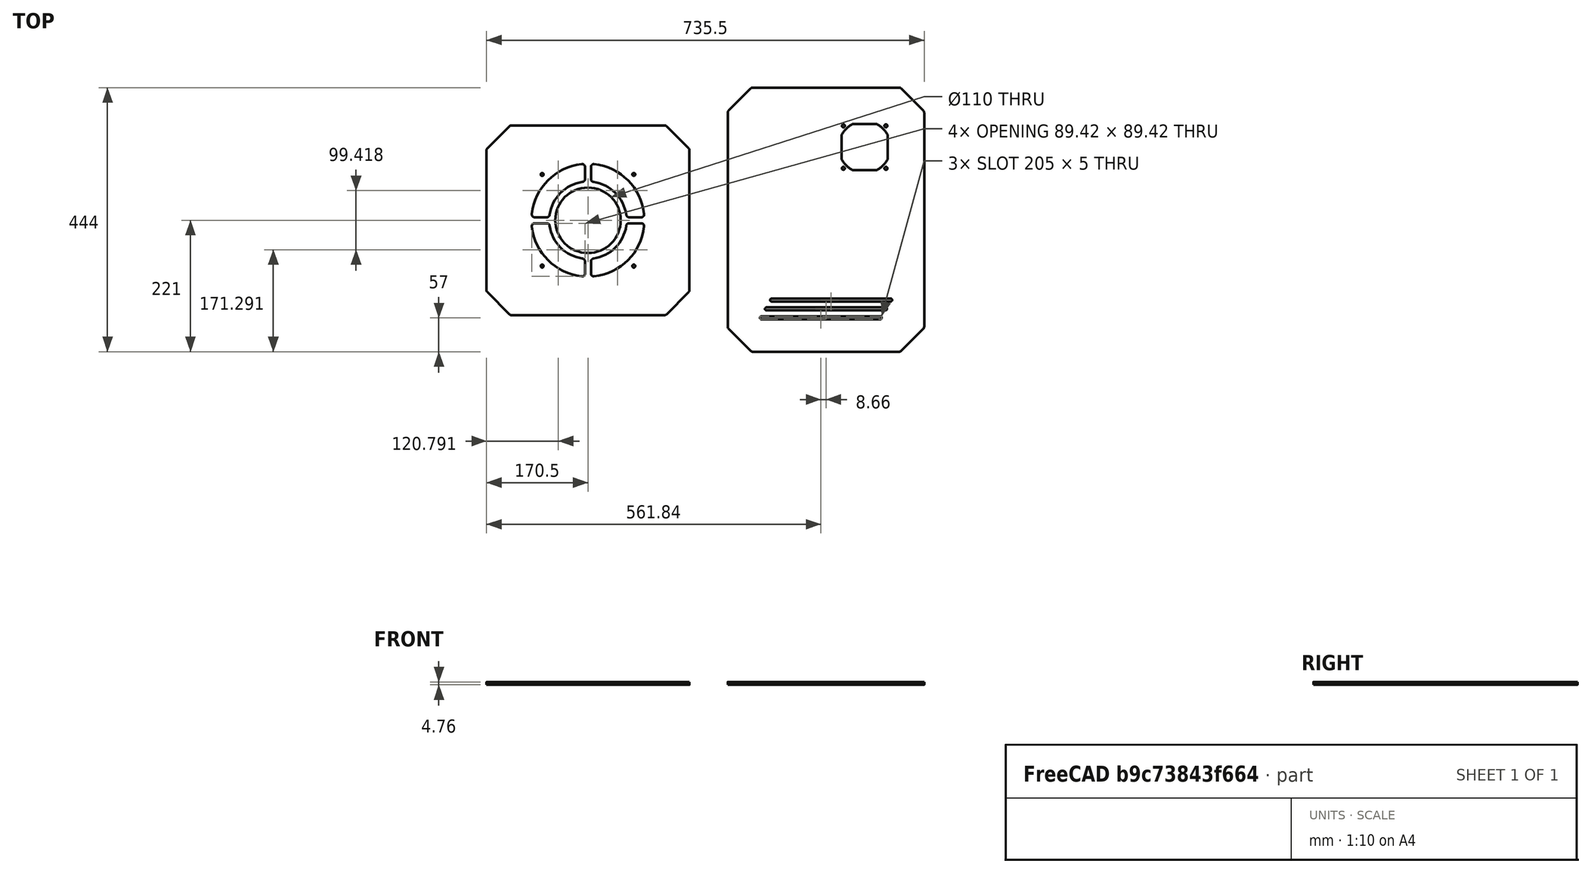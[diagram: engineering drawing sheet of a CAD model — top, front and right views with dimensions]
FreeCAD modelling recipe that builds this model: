
FCSTD DOCUMENT  (FreeCAD 0.19R23578 (Git))
Label: enclosure_windows
License: All rights reserved
LicenseURL: http://en.wikipedia.org/wiki/All_rights_reserved
objects: TechDraw::DrawViewDimExtent×4, PartDesign::CoordinateSystem×4, Sketcher::SketchObject×2, TechDraw::DrawViewPart×2, PartDesign::Pad×2, TechDraw::DrawRichAnno×2, PartDesign::Body×2, TechDraw::DrawSVGTemplate×1, PartDesign::Fillet×1, TechDraw::DrawPage×1
note: 14 computed .brp shape members not serialized (recipe doc carries the construction recipe); baked Part::Feature solids carry a one-line shape summary decoded from their .brp

FEATURE [Sketcher::SketchObject] Sketch001  label="side_piece"
  AttachmentOffset = pos=(400,1,0) rot=(0,0,1;0rad)
  MapMode = 5
  Placement = pos=(400,1,0) rot=(0,0,1;0rad)
  Support = -> [XY_Plane]
  sketch-geometry (52):
    g0: LineSegment StartX=-165 StartY=180 StartZ=0 EndX=-165 EndY=-180 EndZ=0
    g1: LineSegment StartX=-163.536 StartY=-183.536 StartZ=0 EndX=-126.536 EndY=-220.536 EndZ=0
    g2: LineSegment StartX=-123 StartY=-222 StartZ=0 EndX=123 EndY=-222 EndZ=0
    g3: LineSegment StartX=126.536 StartY=-220.536 StartZ=0 EndX=163.536 EndY=-183.536 EndZ=0
    g4: LineSegment StartX=165 StartY=-180 StartZ=0 EndX=165 EndY=180 EndZ=0
    g5: LineSegment StartX=163.536 StartY=183.536 StartZ=0 EndX=126.536 EndY=220.536 EndZ=0
    g6: LineSegment StartX=123 StartY=222 StartZ=0 EndX=-123 EndY=222 EndZ=0
    g7: LineSegment StartX=-126.536 StartY=220.536 StartZ=0 EndX=-163.536 EndY=183.536 EndZ=0
    g8: LineSegment StartX=-108.66 StartY=-165 StartZ=0 EndX=-91.3397 EndY=-135 EndZ=0
    g9: LineSegment StartX=-91.3397 StartY=-135 StartZ=0 EndX=108.66 EndY=-135 EndZ=0
    g10: LineSegment StartX=91.3397 StartY=-165 StartZ=0 EndX=-108.66 EndY=-165 EndZ=0
    g11: ArcOfCircle CenterX=-91.3397 CenterY=-135 CenterZ=0 NormalX=0 NormalY=0 NormalZ=1 AngleXU=0 Radius=2.5 StartAngle=1.5708 EndAngle=4.71239
    g12: ArcOfCircle CenterX=108.66 CenterY=-135 CenterZ=0 NormalX=0 NormalY=0 NormalZ=1 AngleXU=0 Radius=2.5 StartAngle=4.71239 EndAngle=7.85398
    g13: LineSegment StartX=-91.3397 StartY=-137.5 StartZ=0 EndX=108.66 EndY=-137.5 EndZ=0
    g14: LineSegment StartX=-91.3397 StartY=-132.5 StartZ=0 EndX=108.66 EndY=-132.5 EndZ=0
    g15: ArcOfCircle CenterX=-100 CenterY=-150 CenterZ=0 NormalX=0 NormalY=0 NormalZ=1 AngleXU=0 Radius=2.5 StartAngle=1.5708 EndAngle=4.71239
    g16: ArcOfCircle CenterX=100 CenterY=-150 CenterZ=0 NormalX=0 NormalY=0 NormalZ=1 AngleXU=0 Radius=2.5 StartAngle=4.71239 EndAngle=7.85398
    g17: LineSegment StartX=-100 StartY=-152.5 StartZ=0 EndX=100 EndY=-152.5 EndZ=0
    g18: LineSegment StartX=-100 StartY=-147.5 StartZ=0 EndX=100 EndY=-147.5 EndZ=0
    g19: ArcOfCircle CenterX=-108.66 CenterY=-165 CenterZ=0 NormalX=0 NormalY=0 NormalZ=1 AngleXU=0 Radius=2.5 StartAngle=1.5708 EndAngle=4.71239
    g20: ArcOfCircle CenterX=91.3397 CenterY=-165 CenterZ=0 NormalX=0 NormalY=0 NormalZ=1 AngleXU=0 Radius=2.5 StartAngle=4.71239 EndAngle=7.85398
    g21: LineSegment StartX=-108.66 StartY=-167.5 StartZ=0 EndX=91.3397 EndY=-167.5 EndZ=0
    g22: LineSegment StartX=-108.66 StartY=-162.5 StartZ=0 EndX=91.3397 EndY=-162.5 EndZ=0
    g23: LineSegment StartX=44.2199 StartY=160.5 StartZ=0 EndX=85.7801 EndY=160.5 EndZ=0
    g24: LineSegment StartX=103.5 StartY=101.22 StartZ=0 EndX=103.5 EndY=142.78 EndZ=0
    g25: LineSegment StartX=85.7801 StartY=83.5 StartZ=0 EndX=44.2199 EndY=83.5 EndZ=0
    g26: LineSegment StartX=26.5 StartY=101.22 StartZ=0 EndX=26.5 EndY=142.78 EndZ=0
    g27: ArcOfCircle CenterX=65 CenterY=122 CenterZ=0 NormalX=0 NormalY=0 NormalZ=1 AngleXU=0 Radius=43.75 StartAngle=5.20732 EndAngle=5.78825
    g28: ArcOfCircle CenterX=65 CenterY=122 CenterZ=0 NormalX=0 NormalY=0 NormalZ=1 AngleXU=0 Radius=43.75 StartAngle=0.494934 EndAngle=1.07586
    g29: ArcOfCircle CenterX=65 CenterY=122 CenterZ=0 NormalX=0 NormalY=0 NormalZ=1 AngleXU=0 Radius=43.75 StartAngle=2.06573 EndAngle=2.64666
    g30: ArcOfCircle CenterX=65 CenterY=122 CenterZ=0 NormalX=0 NormalY=0 NormalZ=1 AngleXU=0 Radius=43.75 StartAngle=3.63653 EndAngle=4.21745
    g31: LineSegment StartX=29.25 StartY=157.75 StartZ=0 EndX=100.75 EndY=157.75 EndZ=0
    g32: LineSegment StartX=100.75 StartY=157.75 StartZ=0 EndX=100.75 EndY=86.25 EndZ=0
    g33: LineSegment StartX=100.75 StartY=86.25 StartZ=0 EndX=29.25 EndY=86.25 EndZ=0
    g34: LineSegment StartX=29.25 StartY=86.25 StartZ=0 EndX=29.25 EndY=157.75 EndZ=0
    g35: LineSegment StartX=29.25 StartY=157.75 StartZ=0 EndX=100.75 EndY=86.25 EndZ=0
    g36: LineSegment StartX=100.75 StartY=157.75 StartZ=0 EndX=29.25 EndY=86.25 EndZ=0
    g37: Circle CenterX=29.25 CenterY=157.75 CenterZ=0 NormalX=0 NormalY=0 NormalZ=1 AngleXU=0 Radius=2.5
    g38: Circle CenterX=100.75 CenterY=157.75 CenterZ=0 NormalX=0 NormalY=0 NormalZ=1 AngleXU=0 Radius=2.5
    g39: Circle CenterX=100.75 CenterY=86.25 CenterZ=0 NormalX=0 NormalY=0 NormalZ=1 AngleXU=0 Radius=2.5
    g40: Circle CenterX=29.25 CenterY=86.25 CenterZ=0 NormalX=0 NormalY=0 NormalZ=1 AngleXU=0 Radius=2.5
    g41: LineSegment StartX=108.66 StartY=-135 StartZ=0 EndX=100 EndY=-150 EndZ=0
    g42: LineSegment StartX=100 StartY=-150 StartZ=0 EndX=91.3397 EndY=-165 EndZ=0
    g43: ArcOfCircle CenterX=-123 CenterY=217 CenterZ=0 NormalX=0 NormalY=0 NormalZ=1 AngleXU=0 Radius=5 StartAngle=1.5708 EndAngle=2.35619
    g44: ArcOfCircle CenterX=-160 CenterY=180 CenterZ=0 NormalX=0 NormalY=0 NormalZ=1 AngleXU=0 Radius=5 StartAngle=2.35619 EndAngle=3.14159
    g45: ArcOfCircle CenterX=123 CenterY=217 CenterZ=0 NormalX=0 NormalY=0 NormalZ=1 AngleXU=0 Radius=5 StartAngle=0.785398 EndAngle=1.5708
    g46: ArcOfCircle CenterX=160 CenterY=180 CenterZ=0 NormalX=0 NormalY=0 NormalZ=1 AngleXU=0 Radius=5 StartAngle=5e-16 EndAngle=0.785398
    g47: ArcOfCircle CenterX=160 CenterY=-180 CenterZ=0 NormalX=0 NormalY=0 NormalZ=1 AngleXU=0 Radius=5 StartAngle=5.49779 EndAngle=6.28319
    g48: ArcOfCircle CenterX=123 CenterY=-217 CenterZ=0 NormalX=0 NormalY=0 NormalZ=1 AngleXU=0 Radius=5 StartAngle=4.71239 EndAngle=5.49779
    g49: ArcOfCircle CenterX=-160 CenterY=-180 CenterZ=0 NormalX=0 NormalY=0 NormalZ=1 AngleXU=0 Radius=5 StartAngle=3.14159 EndAngle=3.92699
    g50: ArcOfCircle CenterX=-123 CenterY=-217 CenterZ=0 NormalX=0 NormalY=0 NormalZ=1 AngleXU=0 Radius=5 StartAngle=3.92699 EndAngle=4.71239
    g51: GeomPoint X=308.66 Y=-135 Z=0
  constraints (131):
    c: Horizontal(g2)
    c: Vertical(g4)
    c: Horizontal(g6)
    c: Coincident(g8,g9)
    c: Horizontal(g9)
    c: Coincident(g10,g8)
    c: Horizontal(g10)
    c: Tangent(g11,g14)
    c: Tangent(g11,g13)
    c: Tangent(g13,g12)
    c: Tangent(g14,g12)
    c: Horizontal(g13)
    c: Coincident(g11,g8)
    c: Tangent(g15,g18)
    c: Tangent(g15,g17)
    c: Tangent(g17,g16)
    c: Tangent(g18,g16)
    c: Horizontal(g17)
    c: PointOnObject(g15,g8)
    c: Tangent(g19,g22)
    c: Tangent(g19,g21)
    c: Tangent(g21,g20)
    c: Tangent(g22,g20)
    c: Horizontal(g21)
    c: Coincident(g19,g8)
    c: Horizontal(g23)
    c: Horizontal(g25)
    c: Vertical(g24)
    c: Vertical(g26)
    c: PointOnObject(g23,g27)
    c: PointOnObject(g26,g27)
    c: PointOnObject(g23,g27)
    c: PointOnObject(g26,g27)
    c: Coincident(g27,g25)
    c: Coincident(g30,g25)
    c: Equal(g27,g28)
    c: Coincident(g27,g24)
    c: Coincident(g28,g24)
    c: Coincident(g27,g28)
    c: Equal(g28,g29)
    c: PointOnObject(g28,g23)
    c: PointOnObject(g29,g23)
    c: Coincident(g28,g29)
    c: Equal(g29,g30)
    c: PointOnObject(g29,g26)
    c: PointOnObject(g30,g26)
    c: Coincident(g29,g30)
    c: Equal(g26,g23)
    c: Equal(g23,g24)
    c: Equal(g24,g25)
    c: Diameter(g29) = 87.5
    c: DistanceY(g25,g23) = 77
    c: Coincident(g31,g32)
    c: Coincident(g32,g33)
    c: Coincident(g33,g34)
    c: Coincident(g34,g31)
    c: Horizontal(g31)
    c: Horizontal(g33)
    c: Vertical(g32)
    c: Vertical(g34)
    c: Coincident(g35,g31)
    c: Coincident(g35,g32)
    c: Coincident(g36,g31)
    c: Coincident(g36,g33)
    c: PointOnObject(g27,g36)
    c: PointOnObject(g27,g35)
    c: Equal(g31,g34)
    c: DistanceY(g34,g34) = 71.5
    c: Coincident(g37,g31)
    c: Coincident(g38,g31)
    c: Coincident(g39,g32)
    c: Coincident(g40,g33)
    c: Equal(g40,g37)
    c: Equal(g37,g38)
    c: Equal(g38,g39)
    c: Diameter(g38) = 5
    c: Vertical(g0)
    c: Coincident(g12,g9)
    c: Equal(g20,g16)
    c: Equal(g16,g12)
    c: DistanceY(g12,g12) = 5
    c: Coincident(g41,g12)
    c: Coincident(g41,g16)
    c: Coincident(g42,g16)
    c: Coincident(g42,g20)
    c: Equal(g41,g42)
    c: Parallel(g41,g42)
    c: DistanceY(g19,g11) = 30
    c: Angle(g10,g8) = 1.0472
    c: Angle(g42,g10) = 2.0944
    c: Coincident(g10,g20)
    c: Tangent(g6,g43) = -1.5708
    c: Tangent(g7,g43) = -1.5708
    c: Tangent(g0,g44) = -1.5708
    c: Tangent(g7,g44) = -1.5708
    c: Tangent(g5,g45) = -1.5708
    c: Tangent(g6,g45) = -1.5708
    c: Tangent(g4,g46) = -1.5708
    c: Tangent(g5,g46) = -1.5708
    c: Tangent(g3,g47) = -1.5708
    c: Tangent(g4,g47) = -1.5708
    c: Tangent(g2,g48) = -1.5708
    c: Tangent(g3,g48) = -1.5708
    c: Tangent(g0,g49) = -1.5708
    c: Tangent(g1,g49) = -1.5708
    c: Tangent(g1,g50) = -1.5708
    c: Tangent(g2,g50) = -1.5708
    c: Equal(g44,g43)
    c: Equal(g43,g45)
    c: Equal(g45,g46)
    c: Equal(g46,g47)
    c: Equal(g47,g48)
    c: Equal(g48,g50)
    c: Equal(g50,g49)
    c: Radius(g49) = 5
    c: Parallel(g7,g3)
    c: Parallel(g5,g1)
    c: Perpendicular(g5,g7)
    c: DistanceX(g0,g4) = 330
    c: Symmetric(g0,g4,g-2)
    c: Symmetric(g6,g2,g-1)
    c: DistanceY(g2,g6) = 444
    c: Angle(g6,g5) = 2.35619
    c: Equal(g3,g1)
    c: DistanceX(g0,g2) = 42
    c: DistanceX(g9,g9) = 200
    c: Symmetric(g11,g51,g12)
    c: Symmetric(g15,g16,g-2)
    c: DistanceY(g16,g-1) = 150
    c: DistanceY(g27,g6) = 100
    c: DistanceX(g27,g4) = 100
FEATURE [TechDraw::DrawSVGTemplate] Template
  EditableTexts = Author=AN; DWG_num=x; Date=06/08/2020; Revision=1; Scale=1:4; Subtitle=Material: 3/16" Arrylic sheet; Title=Enclosure window panels
  Height = 215.9
  Orientation = 1
  Width = 279.4
FEATURE [TechDraw::DrawViewPart] View
  CoarseView = false
  Direction = (0,0,1)
  Focus = 100
  HardHidden = false
  IsoCount = 0
  IsoHidden = false
  IsoVisible = false
  LockPosition = false
  Perspective = false
  Rotation = 0
  Scale = 0.25
  ScaleType = 0
  SeamHidden = false
  SeamVisible = true
  SmoothHidden = false
  SmoothVisible = true
  Source = -> [Sketch001]
  X = 209.743
  XDirection = (1,0,0)
  Y = 125.367
FEATURE [PartDesign::Pad] Pad
  Direction = (1,1,1)
  Length = 4.7625
  Length2 = 100
  Midplane = true
  Profile = -> Sketch001
  Type = 0
  expr: Length = 3in / 16
FEATURE [Sketcher::SketchObject] Sketch002  label="top_piece001"
  MapMode = 5
  Support = -> [XY_Plane001]
  sketch-geometry (41):
    g0: LineSegment StartX=-170.5 StartY=117.5 StartZ=0 EndX=-170.5 EndY=-117.5 EndZ=0
    g1: LineSegment StartX=-169.036 StartY=-121.036 StartZ=0 EndX=-132.036 EndY=-158.036 EndZ=0
    g2: LineSegment StartX=-128.5 StartY=-159.5 StartZ=0 EndX=128.5 EndY=-159.5 EndZ=0
    g3: LineSegment StartX=132.036 StartY=-158.036 StartZ=0 EndX=169.036 EndY=-121.036 EndZ=0
    g4: LineSegment StartX=170.5 StartY=-117.5 StartZ=0 EndX=170.5 EndY=117.5 EndZ=0
    g5: LineSegment StartX=169.036 StartY=121.036 StartZ=0 EndX=132.036 EndY=158.036 EndZ=0
    g6: LineSegment StartX=128.5 StartY=159.5 StartZ=0 EndX=-128.5 EndY=159.5 EndZ=0
    g7: LineSegment StartX=-132.036 StartY=158.036 StartZ=0 EndX=-169.036 EndY=121.036 EndZ=0
    g8: Circle CenterX=0 CenterY=0 CenterZ=0 NormalX=0 NormalY=0 NormalZ=1 AngleXU=0 Radius=55
    g9: ArcOfCircle CenterX=128.5 CenterY=154.5 CenterZ=0 NormalX=0 NormalY=0 NormalZ=1 AngleXU=0 Radius=5 StartAngle=0.785398 EndAngle=1.5708
    g10: ArcOfCircle CenterX=165.5 CenterY=117.5 CenterZ=0 NormalX=0 NormalY=0 NormalZ=1 AngleXU=0 Radius=5 StartAngle=1.4e-15 EndAngle=0.785398
    g11: ArcOfCircle CenterX=165.5 CenterY=-117.5 CenterZ=0 NormalX=0 NormalY=0 NormalZ=1 AngleXU=0 Radius=5 StartAngle=5.49779 EndAngle=6.28319
    g12: ArcOfCircle CenterX=128.5 CenterY=-154.5 CenterZ=0 NormalX=0 NormalY=0 NormalZ=1 AngleXU=0 Radius=5 StartAngle=4.71239 EndAngle=5.49779
    g13: ArcOfCircle CenterX=-128.5 CenterY=-154.5 CenterZ=0 NormalX=0 NormalY=0 NormalZ=1 AngleXU=0 Radius=5 StartAngle=3.92699 EndAngle=4.71239
    g14: ArcOfCircle CenterX=-165.5 CenterY=-117.5 CenterZ=0 NormalX=0 NormalY=0 NormalZ=1 AngleXU=0 Radius=5 StartAngle=3.14159 EndAngle=3.92699
    g15: ArcOfCircle CenterX=-128.5 CenterY=154.5 CenterZ=0 NormalX=0 NormalY=0 NormalZ=1 AngleXU=0 Radius=5 StartAngle=1.5708 EndAngle=2.35619
    g16: ArcOfCircle CenterX=-165.5 CenterY=117.5 CenterZ=0 NormalX=0 NormalY=0 NormalZ=1 AngleXU=0 Radius=5 StartAngle=2.35619 EndAngle=3.14159
    g17: LineSegment StartX=-94.8683 StartY=5 StartZ=0 EndX=-64.8074 EndY=5 EndZ=0
    g18: LineSegment StartX=94.8683 StartY=-5 StartZ=0 EndX=64.8074 EndY=-5 EndZ=0
    g19: LineSegment StartX=-5 StartY=94.8683 StartZ=0 EndX=-5 EndY=64.8074 EndZ=0
    g20: LineSegment StartX=5 StartY=94.8683 StartZ=0 EndX=5 EndY=64.8074 EndZ=0
    g21: ArcOfCircle CenterX=0 CenterY=0 CenterZ=0 NormalX=0 NormalY=0 NormalZ=1 AngleXU=0 Radius=65 StartAngle=1.6478 EndAngle=3.06459
    g22: ArcOfCircle CenterX=0 CenterY=0 CenterZ=0 NormalX=0 NormalY=0 NormalZ=1 AngleXU=0 Radius=95 StartAngle=1.62345 EndAngle=3.08894
    g23: LineSegment StartX=64.8074 StartY=5 StartZ=0 EndX=94.8683 EndY=5 EndZ=0
    g24: LineSegment StartX=-5 StartY=-64.8074 StartZ=0 EndX=-5 EndY=-94.8683 EndZ=0
    g25: LineSegment StartX=-64.8074 StartY=-5 StartZ=0 EndX=-94.8683 EndY=-5 EndZ=0
    g26: LineSegment StartX=5 StartY=-64.8074 StartZ=0 EndX=5 EndY=-94.8683 EndZ=0
    g27: ArcOfCircle CenterX=0 CenterY=0 CenterZ=0 NormalX=0 NormalY=0 NormalZ=1 AngleXU=0 Radius=95 StartAngle=0.0526559 EndAngle=1.51814
    g28: ArcOfCircle CenterX=0 CenterY=0 CenterZ=0 NormalX=0 NormalY=0 NormalZ=1 AngleXU=0 Radius=65 StartAngle=0.0769991 EndAngle=1.4938
    g29: ArcOfCircle CenterX=0 CenterY=0 CenterZ=0 NormalX=0 NormalY=0 NormalZ=1 AngleXU=0 Radius=65 StartAngle=3.21859 EndAngle=4.63539
    g30: ArcOfCircle CenterX=0 CenterY=0 CenterZ=0 NormalX=0 NormalY=0 NormalZ=1 AngleXU=0 Radius=95 StartAngle=3.19425 EndAngle=4.65973
    g31: ArcOfCircle CenterX=0 CenterY=0 CenterZ=0 NormalX=0 NormalY=0 NormalZ=1 AngleXU=0 Radius=65 StartAngle=4.78939 EndAngle=6.20619
    g32: ArcOfCircle CenterX=0 CenterY=0 CenterZ=0 NormalX=0 NormalY=0 NormalZ=1 AngleXU=0 Radius=95 StartAngle=4.76504 EndAngle=6.23053
    g33: Circle CenterX=-77 CenterY=77 CenterZ=0 NormalX=0 NormalY=0 NormalZ=1 AngleXU=0 Radius=2.5
    g34: Circle CenterX=77 CenterY=-77 CenterZ=0 NormalX=0 NormalY=0 NormalZ=1 AngleXU=0 Radius=2.5
    g35: Circle CenterX=-77 CenterY=-77 CenterZ=0 NormalX=0 NormalY=0 NormalZ=1 AngleXU=0 Radius=2.5
    g36: Circle CenterX=77 CenterY=77 CenterZ=0 NormalX=0 NormalY=0 NormalZ=1 AngleXU=0 Radius=2.5
    g37: LineSegment StartX=-77 StartY=77 StartZ=0 EndX=77 EndY=77 EndZ=0
    g38: LineSegment StartX=77 StartY=77 StartZ=0 EndX=77 EndY=-77 EndZ=0
    g39: LineSegment StartX=77 StartY=-77 StartZ=0 EndX=-77 EndY=-77 EndZ=0
    g40: LineSegment StartX=-77 StartY=-77 StartZ=0 EndX=-77 EndY=77 EndZ=0
  constraints (100):
    c: Vertical(g0)
    c: Horizontal(g2)
    c: Vertical(g4)
    c: Horizontal(g6)
    c: Coincident(g8,g-1)
    c: Tangent(g5,g9) = -1.5708
    c: Tangent(g6,g9) = -1.5708
    c: Tangent(g4,g10) = -1.5708
    c: Tangent(g5,g10) = -1.5708
    c: Tangent(g3,g11) = -1.5708
    c: Tangent(g4,g11) = -1.5708
    c: Tangent(g2,g12) = -1.5708
    c: Tangent(g3,g12) = -1.5708
    c: Tangent(g1,g13) = -1.5708
    c: Tangent(g2,g13) = -1.5708
    c: Tangent(g0,g14) = -1.5708
    c: Tangent(g1,g14) = -1.5708
    c: Tangent(g6,g15) = -1.5708
    c: Tangent(g7,g15) = -1.5708
    c: Tangent(g0,g16) = -1.5708
    c: Tangent(g7,g16) = -1.5708
    c: Parallel(g5,g1)
    c: Parallel(g7,g3)
    c: Perpendicular(g5,g7)
    c: Angle(g7,g6) = 2.35619
    c: Equal(g7,g5)
    c: Equal(g5,g3)
    c: Equal(g3,g1)
    c: Symmetric(g0,g4,g-2)
    c: Symmetric(g6,g2,g-1)
    c: Equal(g14,g13)
    c: Equal(g13,g12)
    c: Equal(g12,g11)
    c: Equal(g11,g10)
    c: Equal(g10,g9)
    c: Radius(g10) = 5
    c: DistanceX(g0,g6) = 42
    c: DistanceX(g0,g4) = 341
    c: DistanceY(g2,g6) = 319
    c: Horizontal(g17)
    c: Horizontal(g18)
    c: Vertical(g19)
    c: Vertical(g20)
    c: Diameter(g8) = 110
    c: Coincident(g21,g8)
    c: Coincident(g22,g8)
    c: Tangent(g17,g23)
    c: Tangent(g19,g24)
    c: Tangent(g18,g25)
    c: Tangent(g20,g26)
    c: Coincident(g21,g19)
    c: Coincident(g28,g20)
    c: Coincident(g22,g27)
    c: Equal(g21,g28)
    c: Coincident(g21,g28)
    c: Coincident(g23,g28)
    c: Coincident(g18,g31)
    c: Coincident(g18,g32)
    c: Coincident(g23,g27)
    c: Coincident(g19,g22)
    c: Coincident(g20,g27)
    c: Equal(g21,g29)
    c: Coincident(g21,g17)
    c: Coincident(g21,g29)
    c: Equal(g22,g30)
    c: Coincident(g22,g30)
    c: Coincident(g17,g22)
    c: Coincident(g25,g30)
    c: Coincident(g25,g29)
    c: Equal(g29,g31)
    c: Coincident(g29,g24)
    c: Coincident(g31,g26)
    c: Coincident(g29,g31)
    c: Coincident(g30,g32)
    c: Coincident(g26,g32)
    c: Coincident(g24,g30)
    c: Symmetric(g20,g19,g-2)
    c: Diameter(g28) = 130
    c: Diameter(g27) = 190
    c: Symmetric(g18,g23,g-1)
    c: DistanceY(g18,g23) = 10
    c: DistanceX(g19,g20) = 10
    c: Coincident(g37,g38)
    c: Coincident(g38,g39)
    c: Coincident(g39,g40)
    c: Coincident(g40,g37)
    c: Horizontal(g39)
    c: Vertical(g38)
    c: Coincident(g37,g33)
    c: Coincident(g38,g34)
    c: Coincident(g36,g37)
    c: Coincident(g35,g39)
    c: Equal(g40,g39)
    c: Symmetric(g35,g33,g-1)
    c: Symmetric(g33,g36,g-2)
    c: Equal(g36,g33)
    c: Equal(g33,g35)
    c: Equal(g35,g34)
    c: Diameter(g34) = 5
    c: DistanceX(g37,g37) = 154
FEATURE [PartDesign::Pad] Pad001
  Direction = (1,1,1)
  Length = 4.7625
  Length2 = 100
  Midplane = true
  Profile = -> Sketch002
  Type = 0
  expr: Length = 3in / 16
FEATURE [PartDesign::Fillet] Fillet
  Base = -> Pad001 [Edge80,Edge88,Edge89,Edge77,Edge76,Edge59,Edge83,Edge53,Edge52,Edge68,Edge65,Edge56,Edge95,Edge71,Edge64,Edge92]
  BaseFeature = -> Pad001
  Radius = 5
  SupportTransform = true
FEATURE [TechDraw::DrawViewPart] View001
  CoarseView = false
  Direction = (0,0,1)
  Focus = 100
  HardHidden = false
  IsoCount = 0
  IsoHidden = false
  IsoVisible = false
  LockPosition = false
  Perspective = false
  Rotation = 0
  Scale = 0.25
  ScaleType = 0
  SeamHidden = false
  SeamVisible = true
  SmoothHidden = false
  SmoothVisible = true
  Source = -> [Fillet]
  X = 86.9163
  XDirection = (1,0,0)
  Y = 123.25
FEATURE [TechDraw::DrawViewDimExtent] DimExtent
  Arbitrary = false
  ArbitraryTolerances = false
  CosmeticTags = 288ce400-6803-4ff3-8631-b07757546f7d | fa33bd96-712d-4188-b98a-81c6ac7bc85e
  DirExtent = 0
  FormatSpec = %.0f
  FormatSpecOverTolerance = %+.2f
  FormatSpecUnderTolerance = %+.2f
  Inverted = false
  LockPosition = false
  MeasureType = 1
  OverTolerance = 0
  References2D = -> [View001]
  Rotation = 0
  ScaleType = 0
  Source = -> [View001]
  TheoreticalExact = false
  Type = 1
  UnderTolerance = 0
  X = -6.69232
  Y = 53.5385
FEATURE [TechDraw::DrawViewDimExtent] DimExtent001
  Arbitrary = false
  ArbitraryTolerances = false
  CosmeticTags = 8f42bda8-79a3-4fe8-b8ad-edf73163d0b5 | 82f00fcd-74c2-4853-aa97-94300f8e63c0
  DirExtent = 1
  FormatSpec = %.0f
  FormatSpecOverTolerance = %+.2f
  FormatSpecUnderTolerance = %+.2f
  Inverted = false
  LockPosition = false
  MeasureType = 1
  OverTolerance = 0
  References2D = -> [View001]
  Rotation = 0
  ScaleType = 0
  Source = -> [View001]
  TheoreticalExact = false
  Type = 2
  UnderTolerance = 0
  X = -61.6857
  Y = -4.9465
FEATURE [TechDraw::DrawViewDimExtent] DimExtent003
  Arbitrary = false
  ArbitraryTolerances = false
  CosmeticTags = 2a4c7c9a-20be-468c-a347-82470489cc8d | 03f315e3-f9e5-4f8a-bf5f-073e1e309c87
  DirExtent = 1
  FormatSpec = %.0f
  FormatSpecOverTolerance = %+.2f
  FormatSpecUnderTolerance = %+.2f
  Inverted = false
  LockPosition = false
  MeasureType = 1
  OverTolerance = 0
  References2D = -> [View]
  Rotation = 0
  ScaleType = 0
  Source = -> [View]
  TheoreticalExact = false
  Type = 2
  UnderTolerance = 0
  X = -56.7392
  Y = 5.81941
FEATURE [TechDraw::DrawViewDimExtent] DimExtent004
  Arbitrary = false
  ArbitraryTolerances = false
  CosmeticTags = a94bd8f1-ed9f-4015-9f45-3e27d023ae27 | ae9efa26-c7d3-4067-8a4b-398840287b2f
  DirExtent = 0
  FormatSpec = %.0f
  FormatSpecOverTolerance = %+.2f
  FormatSpecUnderTolerance = %+.2f
  Inverted = false
  LockPosition = false
  MeasureType = 1
  OverTolerance = 0
  References2D = -> [View]
  Rotation = 0
  ScaleType = 0
  Source = -> [View]
  TheoreticalExact = false
  Type = 1
  UnderTolerance = 0
  X = -7.8562
  Y = 65.7593
FEATURE [TechDraw::DrawRichAnno] RichTextAnnotation
  AnnoParent = -> View001
  AnnoText = <!DOCTYPE HTML PUBLIC "-//W3C//DTD HTML 4.0//EN" "http://www.w3.org/TR/REC-html40/strict.dtd">\n<html><head><meta name="qrichtext" content="1" /><style type="text/css">\np, li { white-space: pre-wrap; }\n</style></head><body style=" font-family:'Cantarell'; font-size:10pt; font-weight:400; font-style:normal;">\n<p style=" margin-top:0px; margin-bottom:0px; margin-left:0px; margin-right:0px; -qt-block-indent:0; text-indent:0px;"><span style=" font-family:'Bitstream Vera Sans'; font-size:8pt; text-decoration: underline; color:#000000;">Top panel - 1 Required</span></p>\n<p style=" margin-top:0px; margin-bottom:0px; margin-left:0px; margin-right:0px; -qt-block-indent:0; text-indent:0px;"><span style=" font-family:'Bitstream Vera Sans'; font-size:8pt; color:#000000;">     top_panel.dxf</span></p></body></html>
  LockPosition = false
  MaxWidth = -1
  Rotation = 0
  ScaleType = 0
  ShowFrame = false
  X = -1.16388
  Y = -56.1573
FEATURE [TechDraw::DrawRichAnno] RichTextAnnotation001
  AnnoParent = -> View
  AnnoText = <!DOCTYPE HTML PUBLIC "-//W3C//DTD HTML 4.0//EN" "http://www.w3.org/TR/REC-html40/strict.dtd">\n<html><head><meta name="qrichtext" content="1" /><style type="text/css">\np, li { white-space: pre-wrap; }\n</style></head><body style=" font-family:'Cantarell'; font-size:10pt; font-weight:400; font-style:normal;">\n<p style=" margin-top:0px; margin-bottom:0px; margin-left:0px; margin-right:0px; -qt-block-indent:0; text-indent:0px;"><span style=" font-family:'Bitstream Vera Sans'; font-size:8pt; text-decoration: underline; color:#000000;">Side panel - 2 Required</span></p>\n<p style=" margin-top:0px; margin-bottom:0px; margin-left:0px; margin-right:0px; -qt-block-indent:0; text-indent:0px;"><span style=" font-family:'Bitstream Vera Sans'; font-size:8pt; color:#000000;">    side_panel.dxf</span></p></body></html>
  LockPosition = false
  MaxWidth = -1
  Rotation = 0
  ScaleType = 0
  ShowFrame = false
  X = 2.32776
  Y = -66.3412
FEATURE [TechDraw::DrawPage] Page
  KeepUpdated = false
  NextBalloonIndex = 1
  ProjectionType = 0
  Template = -> Template
  Views = -> [View,View001,DimExtent,DimExtent001,DimExtent003,DimExtent004,RichTextAnnotation,RichTextAnnotation001]
FEATURE [PartDesign::CoordinateSystem] LCS_1
  AttacherType = Attacher::AttachEngine3D
  MapMode = 45
  Placement = pos=(2.625e-13,4.1e-15,0) rot=(0,0,1;0rad)
  Support = -> [Fillet]
FEATURE [PartDesign::Body] Body001  label="top_acrylic_panel"
  Group = -> [Sketch002,Pad001,Fillet,LCS_1]
  Origin = -> Origin001
  Tip = -> Fillet
FEATURE [PartDesign::CoordinateSystem] LCS_2
  AttacherType = Attacher::AttachEngine3D
  MapMode = 45
  Placement = pos=(400,1,0) rot=(0,0,1;0rad)
  Support = -> [Pad]
FEATURE [PartDesign::CoordinateSystem] LCS_3
  AttacherType = Attacher::AttachEngine3D
  MapMode = 45
  Placement = pos=(465,123,2.38125) rot=(0,0,1;0rad)
  Support = -> [Pad]
FEATURE [PartDesign::CoordinateSystem] LCS_4
  AttacherType = Attacher::AttachEngine3D
  MapMode = 45
  Placement = pos=(465,123,-2.38125) rot=(0,0,1;0rad)
  Support = -> [Pad]
FEATURE [PartDesign::Body] Body  label="side_acrylic_panel"
  Group = -> [Sketch001,Pad,LCS_2,LCS_3,LCS_4]
  Origin = -> Origin
  Tip = -> Pad
